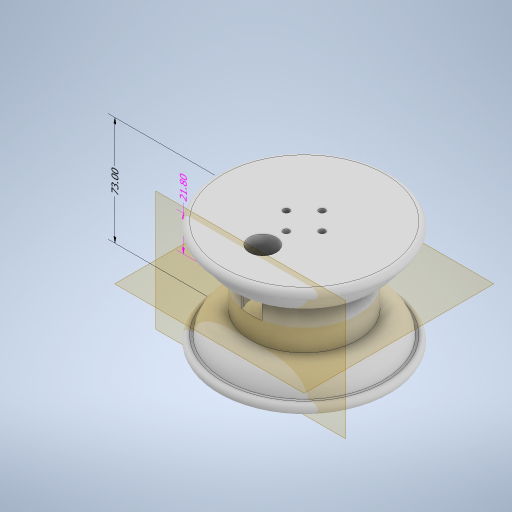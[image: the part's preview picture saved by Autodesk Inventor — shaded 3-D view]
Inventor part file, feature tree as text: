
AUTODESK INVENTOR PART (.ipt)
format: ipt  version: 2023 (Build 270158000, 158)  size: 383,488 bytes
history: native  units: mm
features: extrude x6, sketch x6, other x4, fillet x2, plane x2, mirror x1
ambient origin geometry x8: Origin, YZ Plane, XZ Plane, XY Plane, X Axis, Y Axis, Z Axis, Center Point
bodies: Body1 (feature_tree)
feature tree (21):
  other  "Sólido1"
  other  "Anotaciones"
  extrude  "Extrusión1"  Depth=6.8mm TaperAngle=0.0deg
  fillet  "Empalme1"  Radius=3.4mm
  extrude  "Extrusión2"  Depth=15.0mm TaperAngle=0.0deg
  extrude  "Extrusión3"  Depth=29.4mm TaperAngle=0.0deg
  plane  "Plano de trabajo1"
  fillet  "Empalme3"  Radius=17.0mm
  mirror  "Simetría1"
  extrude  "Extrusión4"  Depth=4.2mm
  plane  "Plano de trabajo2"
  sketch  "Boceto5"  dims[d22=40.0mm d24=360.0deg d26=75.0mm d27=0.0mm]
  extrude  "Extrusión5"  Depth=75.0mm TaperAngle=0.0deg
  extrude  "Extrusión6"  Depth=14.0mm
  sketch  "Boceto1"  dims[d0=115.6mm d1=6.8mm d2=0.0mm d3=3.4mm]
  sketch  "Boceto2"  dims[d4=5.0mm d5=15.0mm d6=0.0mm]
  sketch  "Boceto3"  dims[d7=72.0mm d11=29.4mm d12=0.0mm d14=17.0mm]
  sketch  "Boceto4"  dims[d18=24.0mm d19=4.2mm]
  sketch  "Boceto6"  dims[d28=36.0mm d29=14.0mm d30=18.0mm d33=30.0mm d34=36.5mm d35=0.0mm d36=17.25mm d37=0.0mm d10=21.8mm d15=5.307863mm d16=3.17773mm d17=73.0mm d8=3.773034mm d9=6.94347mm]
  other  "Cota lineal 1"
  other  "Cota lineal 2"
